# Revit family: 1Electronics_Commercial-Audio_Biamp_Volume-Control_E-VOL20_E-VOL40_E-VOL60_E-VOL120
name_source: partatom
category: Communication Devices
units: mm (PartAtom-declared; Revit-internal decimal feet)

## family parameters
Cut with Voids When Loaded = No
Host = Face
Maintain Annotation Orientation = No
OmniClass Number = 23.85.10.11.14
OmniClass Title = Audio Equipment
Part Type = Normal
Room Calculation Point = No
Round Connector Dimension = Use Diameter
Shared = No

## types (4) — shared parameters
Connector Description = Euroblock 6-pole
Default Elevation = 4' - 0"
Depth = 0' - 2"
Height = 0' - 3"
Housing Material = Biamp - Plastic - White
Manufacturer = Biamp
Mounting = Screw
Number of Poles = 1
Power Factor = 1
Product Documentation Link = https://downloads.biamp.com
Product Page URL = https://www.biamp.com
Product data url = https://www.bimobject.com
Steps = 0 + 11
Stereo/mono = Mono
URL = https://www.biamp.com
Voltage = 100 V
Weight = 0.741 lb
Width = 0' - 3"

## per-type parameters (varying)
| type | Apparent Load | Description | Max Power Consumption |
| E-VOL20 | 20 VA | E-VOL20 100 Volt, 20 Watts Volume Control, White | 20 W |
| E-VOL40 | 40 VA | E-VOL40 100 Volt, 40 Watts Euro Volume Control, White | 40 W |
| E-VOL60 | 60 VA | E-VOL60 100 Volt, 60 Watts Euro Volume Control, White | 60 W |
| E-VOL120 | 120 VA | E-VOL120 100 Volt, 120 Watts Euro Volume Control, White | 120 W |

note: column(s) folded — value = type name in every type: Model

## geometry (parser evidence)
native form markers: Sweep x2
no freeform markers — native parametric forms only
